# Revit family: Shower-Shower_Door-KOHLER-Fluence-K-702202_1
name_source: partatom
category: Specialty Equipment
units: mm (PartAtom-declared; Revit-internal decimal feet)

## family parameters
Cut with Voids When Loaded = No
Host = Face
OmniClass Number = 23.31.17.17
OmniClass Title = Shower Enclosures
Part Type = Normal
Room Calculation Point = No
Round Connector Dimension = Use Diameter
Shared = No

## types (6) — shared parameters
ADA Compliant = No
Assembly Code = C1030200
Date Modified = 08/15/2022
Default Elevation = 4"
Height = 55 7/16"
Length = 7 1/4"
Manufacturer = Kohler Co.
Master Format 2014 = 10 28 19.16
Master Format 2014 Name = Shower Doors
Material = Premium Metal Construction
Product Documentation Link = https://www.us.kohler.com
Product Name = Fluence
Product Page URL = https://www.us.kohler.com
URL = https://www.us.kohler.com
WaterSense Certified = No

## per-type parameters (varying)
| type | Description | Finish | Model | Secondary Finish | Type |
| Clear Glass, ABV-Anodized Brushed Bronze | 52-57 Inch W x 55 1/2 Inch H Sliding Bath Door With 1/4 Inch Thick Crystal Clear Glass | Kohler-Metal-ABV-Anodized_Brushed_Bronze | K-702202-6L-ABV | Kohler-Glass-L-Crystal_Clear | 1 |
| Clear Glass, MX-Matte Nickel | 52-57 Inch W x 55 1/2 Inch H Sliding Bath Door With 1/4 Inch Thick Crystal Clear Glass | Kohler-Metal-MX-Matte_Nickel | K-702202-6L-MX | Kohler-Glass-L-Crystal_Clear | 2 |
| Clear Glass, SHP-Bright Polished Silver | 52-57 Inch W x 55 1/2 Inch H Sliding Bath Door With 1/4 Inch Thick Crystal Clear Glass | Kohler-Metal-SHP-Bright_Polished_Silver | K-702202-6L-SHP | Kohler-Glass-L-Crystal_Clear | 3 |
| Falling Lines Glass, ABV-Anodized Brushed Bronze | 552-57 Inch W x 55 1/2 Inch H liding Bath Door With 1/4 Inch Thick Falling Lines Glass | Kohler-Metal-ABV-Anodized_Brushed_Bronze | K-702202-6G54-ABV | KOHLER-Glass-G54-Falling_Lines | 4 |
| Falling Lines Glass, MX-Matte Nickel | 552-57 Inch W x 55 1/2 Inch H liding Bath Door With 1/4 Inch Thick Falling Lines Glass | Kohler-Metal-MX-Matte_Nickel | K-702202-6G54-MX | KOHLER-Glass-G54-Falling_Lines | 5 |
| Falling Lines Glass, SHP-Bright Polished Silver | 552-57 Inch W x 55 1/2 Inch H liding Bath Door With 1/4 Inch Thick Falling Lines Glass | Kohler-Metal-SHP-Bright_Polished_Silver | K-702202-6G54-SHP | KOHLER-Glass-G54-Falling_Lines | 6 |

## geometry (parser evidence)
native form markers: Sweep x5
no freeform markers — native parametric forms only
